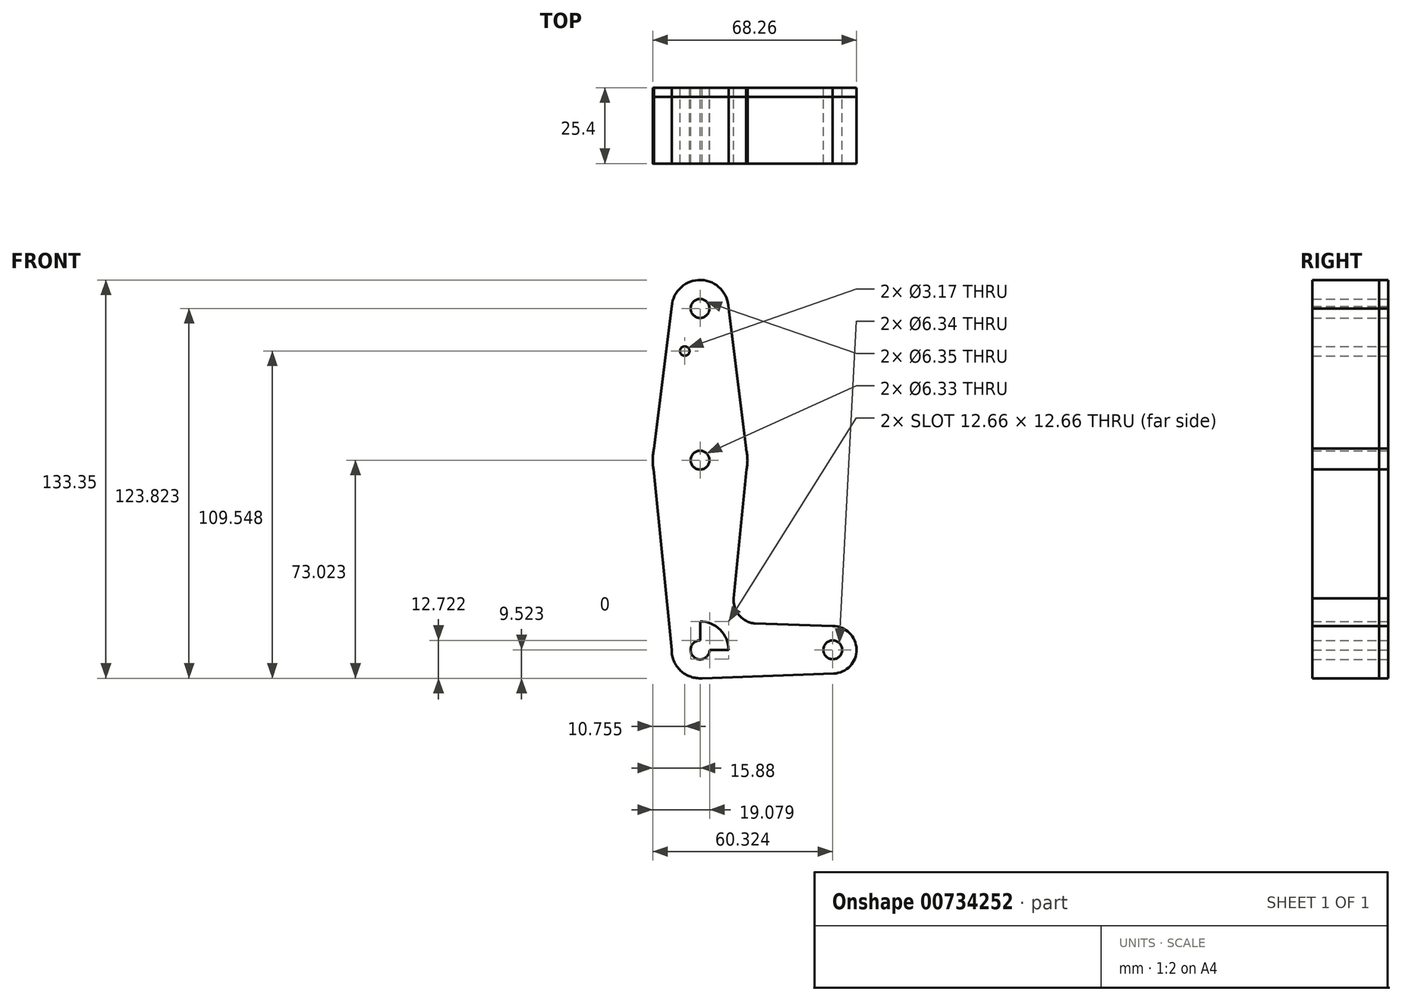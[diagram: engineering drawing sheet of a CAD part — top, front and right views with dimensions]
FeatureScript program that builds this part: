
annotation { "Feature Type Name" : "Feature", "Feature Type Description" : "" }
export const myFeature = defineFeature(function(context is Context, id is Id, definition is map)
    precondition{}
    {
        {
            var Q0;
            Q0=qCreatedBy(makeId("Front.planeOp"),FACE);
            var sketch = newSketch(context, id + "F0", { "sketchPlane" : qUnion([Q0])});
            skLineSegment(sketch, "E0", {"start": v(0, 83.7) * mm, "end": v(0, -30.6) * mm});
            skCircle(sketch, "E1", {"center": v(0, 83.7) * mm, "radius": 9.53 * mm});
            skCircle(sketch, "E2", {"center": v(0, 83.7) * mm, "radius": 3.18 * mm});
            skLineSegment(sketch, "E3", {"start": v(0, -30.6) * mm, "end": v(0, 32.9) * mm});
            skCircle(sketch, "E4", {"center": v(0, 32.9) * mm, "radius": 15.88 * mm});
            skCircle(sketch, "E5", {"center": v(0, -30.6) * mm, "radius": 9.53 * mm});
            skLineSegment(sketch, "E6", {"start": v(0, -30.6) * mm, "end": v(44.44, -30.6) * mm});
            skCircle(sketch, "E7", {"center": v(44.44, -30.6) * mm, "radius": 7.94 * mm});
            skLineSegment(sketch, "E8", {"start": v(-9.5, 84.41) * mm, "end": v(-15.87, 32.9) * mm});
            skLineSegment(sketch, "E9", {"start": v(15.88, 32.9) * mm, "end": v(9.53, 83.7) * mm});
            skLineSegment(sketch, "E10", {"start": v(-15.87, 32.9) * mm, "end": v(-9.53, -30.6) * mm});
            skLineSegment(sketch, "E11", {"start": v(-9.53, -30.6) * mm, "end": v(9.53, -30.6) * mm});
            skLineSegment(sketch, "E12", {"start": v(0, -21.08) * mm, "end": v(0.68, -21.1) * mm});
            skLineSegment(sketch, "E13", {"start": v(0, -40.13) * mm, "end": v(44.73, -38.54) * mm});
            skCircle(sketch, "E14", {"center": v(0, 32.9) * mm, "radius": 3.16 * mm});
            skCircle(sketch, "E15", {"center": v(0, -30.6) * mm, "radius": 3.2 * mm});
            skCircle(sketch, "E16", {"center": v(44.44, -30.6) * mm, "radius": 3.17 * mm});
            skLineSegment(sketch, "E17", {"start": v(0, 32.9) * mm, "end": v(0, 69.42) * mm});
            skCircle(sketch, "E18", {"center": v(-5.12, 69.42) * mm, "radius": 1.59 * mm});
            skArc(sketch, "E19", {"start": v(11.3, -12.89) * mm, "mid": v(12.24, -17.82) * mm, "end": v(15.95, -21.2) * mm});
            skLineSegment(sketch, "E20.trimOffspring", {"start": v(11.25, -13.4) * mm, "end": v(15.88, 32.9) * mm});
            skLineSegment(sketch, "E21.trimOffspring", {"start": v(18.3, -21.74) * mm, "end": v(44.44, -22.67) * mm});
            skPoint(sketch, "E22.visualSharp", {"position": v(17.55, -21.7) * mm});
            skArc(sketch, "E22.filletArc", {"start": v(15.95, -21.2) * mm, "mid": v(17.1, -21.58) * mm, "end": v(18.3, -21.74) * mm});
            skSolve(sketch);
        }
        {
            var Q0;
            Q0 = qSketchRegion(id + "F0", true);
            extrude(context, id + "F1", {"entities" : qUnion([Q0]), "depth" : 25.4 * mm, "offsetDistance" : 25.4 * mm});
        }
        {
            var Q0;
            Q0 = qSketchRegion(id + "F0", true);
            extrude(context, id + "F2", {"entities" : qUnion([Q0]), "depth" : 3.05 * mm, "offsetDistance" : 25.4 * mm});
        }
    });
